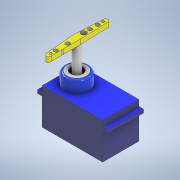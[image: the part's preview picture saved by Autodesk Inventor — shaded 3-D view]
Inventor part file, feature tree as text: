
AUTODESK INVENTOR PART (.ipt)
format: ipt  version: 2021 (Build 250183000, 183)  size: 214,016 bytes
history: native  units: mm
features: extrude x10, sketch x10, fillet x1
ambient origin geometry x8: Origin, YZ Plane, XZ Plane, XY Plane, X Axis, Y Axis, Z Axis, Center Point
bodies: Solid1 (feature_tree)
feature tree (21):
  extrude  "Extrusion1"  Depth=15.0mm
  extrude  "Extrusion2"  Depth=10.0mm
  extrude  "Extrusion3"  Depth=2.0mm TaperAngle=0.0deg
  extrude  "Extrusion4"  Depth=5.0mm
  extrude  "Extrusion5"  Depth=3.0mm
  extrude  "Extrusion6"  Depth=1.0mm
  fillet  "Fillet1"  Radius=2.0mm
  extrude  "Extrusion7"  Depth=2.0mm TaperAngle=0.0deg
  extrude  "Extrusion8"  Depth=5.0mm TaperAngle=0.0deg
  extrude  "Extrusion9"  [1 undecoded]
  extrude  "Extrusion10"  [1 undecoded]
  sketch  "Sketch1"  dims[d0=25.0mm d1=15.0mm]
  sketch  "Sketch2"  dims[d2=15.0mm d3=0.0mm d4=10.0mm]
  sketch  "Sketch3"  dims[d5=5.0mm d6=0.0mm d7=2.0mm d8=0.0mm]
  sketch  "Sketch4"  dims[d9=2.0mm d10=0.0mm d11=5.0mm]
  sketch  "Sketch5"  dims[d12=2.0mm d13=0.0mm d14=3.0mm]
  sketch  "Sketch6"  dims[d15=10.0mm d16=0.0mm d17=1.0mm d18=2.0mm d19=0.0mm]
  sketch  "Sketch7"  dims[d20=12.496mm d22=2.0mm d23=0.0mm]
  sketch  "Sketch8"  dims[d24=5.0mm d25=0.0mm d26=5.0mm d27=0.0mm]
  sketch  "Sketch9"
  sketch  "Sketch10"
note: 2 required parameter values undecoded (feature->parameter linkage not recoverable at this tier; creation-order binding heuristic only, values carry confidence <= 0.55)
